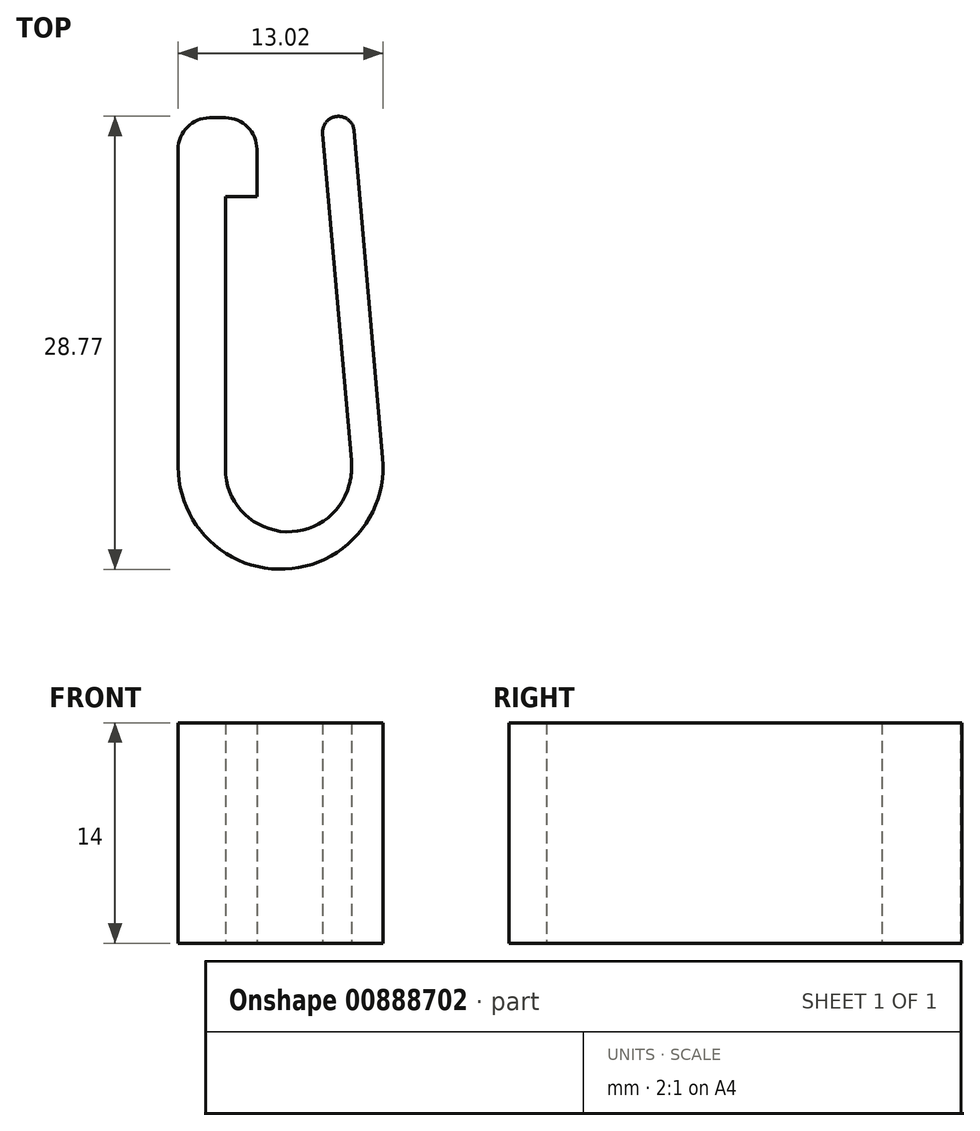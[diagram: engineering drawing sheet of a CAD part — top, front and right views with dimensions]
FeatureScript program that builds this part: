
annotation { "Feature Type Name" : "Feature", "Feature Type Description" : "" }
export const myFeature = defineFeature(function(context is Context, id is Id, definition is map)
    precondition{}
    {
        {
            var Q0;
            Q0=qCreatedBy(makeId("Top.planeOp"),FACE);
            var sketch = newSketch(context, id + "F0", { "sketchPlane" : qUnion([Q0])});
            skLineSegment(sketch, "E0", {"start": v(0, 0) * mm, "end": v(3, 0) * mm});
            skLineSegment(sketch, "E1", {"start": v(5, 2) * mm, "end": v(5, 3) * mm});
            skLineSegment(sketch, "E2", {"start": v(3, 5) * mm, "end": v(-17.17, 5) * mm});
            skLineSegment(sketch, "E3", {"start": v(0, 0) * mm, "end": v(0, 2) * mm});
            skLineSegment(sketch, "E4", {"start": v(0, 2) * mm, "end": v(-17.3, 2) * mm});
            skLineSegment(sketch, "E5", {"start": v(4, -4.18) * mm, "end": v(-16.78, -6) * mm});
            skLineSegment(sketch, "E6", {"start": v(4.18, -6.17) * mm, "end": v(-16.6, -8) * mm});
            skLineSegment(sketch, "E7", {"start": v(5.09, -5.1) * mm, "end": v(5.09, -5.1) * mm});
            skArc(sketch, "E8", {"start": v(-18.33, -5.87) * mm, "mid": v(-17.56, -6) * mm, "end": v(-16.78, -6) * mm});
            skArc(sketch, "E9", {"start": v(-17.17, 5) * mm, "mid": v(-23.67, -1.8) * mm, "end": v(-16.6, -8) * mm});
            skPoint(sketch, "E10.visualSharp", {"position": v(5, -4.1) * mm});
            skArc(sketch, "E10.filletArc", {"start": v(5.09, -5.1) * mm, "mid": v(4.73, -4.41) * mm, "end": v(4, -4.18) * mm});
            skPoint(sketch, "E11.visualSharp", {"position": v(5.17, -6.09) * mm});
            skArc(sketch, "E11.filletArc", {"start": v(4.18, -6.17) * mm, "mid": v(4.86, -5.82) * mm, "end": v(5.09, -5.1) * mm});
            skPoint(sketch, "E12.visualSharp", {"position": v(5, 0) * mm});
            skArc(sketch, "E12.filletArc", {"start": v(3, 0) * mm, "mid": v(4.41, 0.59) * mm, "end": v(5, 2) * mm});
            skPoint(sketch, "E13.visualSharp", {"position": v(5, 5) * mm});
            skArc(sketch, "E13.filletArc", {"start": v(5, 3) * mm, "mid": v(4.41, 4.41) * mm, "end": v(3, 5) * mm});
            skPoint(sketch, "E14.visualSharp", {"position": v(-20, 2) * mm});
            skArc(sketch, "E14.filletArc", {"start": v(-17.3, 2) * mm, "mid": v(-21.27, -1.48) * mm, "end": v(-18.33, -5.87) * mm});
            skSolve(sketch);
        }
        {
            var Q0;
            Q0=makeQuery(id+"F0.imprint","IMPRINT",FACE,{"disambiguationData":[TD([[makeQuery(id+"F0.imprint","IMPRINT",EDGE,{"derivedFrom":sQuery(id+"F0.wireOp",EDGE,"E0")}),1.0]])]});
            extrude(context, id + "F1", {"entities" : qUnion([Q0]), "depth" : 14 * mm, "offsetDistance" : 25 * mm});
        }
        {
            var Q0;
            Q0=makeQuery(id+"F1.opExtrude","SWEPT_BODY",BODY,{"disambiguationData":[OSD([sQuery(id+"F0.wireOp",EDGE,"E0"),sQuery(id+"F0.wireOp",EDGE,"E1"),sQuery(id+"F0.wireOp",EDGE,"E2"),sQuery(id+"F0.wireOp",EDGE,"E3"),sQuery(id+"F0.wireOp",EDGE,"E4"),sQuery(id+"F0.wireOp",EDGE,"E5"),sQuery(id+"F0.wireOp",EDGE,"E6"),sQuery(id+"F0.wireOp",EDGE,"E8"),sQuery(id+"F0.wireOp",EDGE,"E9"),sQuery(id+"F0.wireOp",EDGE,"E10.filletArc"),sQuery(id+"F0.wireOp",EDGE,"E11.filletArc"),sQuery(id+"F0.wireOp",EDGE,"E12.filletArc"),sQuery(id+"F0.wireOp",EDGE,"E13.filletArc"),sQuery(id+"F0.wireOp",EDGE,"E14.filletArc")])]});
            var Q1;
            Q1=makeQuery(id+"F1.opExtrude","SWEPT_EDGE",EDGE,{"disambiguationData":[OSD([sQuery(id+"F0.wireOp",EDGE,"E3"),sQuery(id+"F0.wireOp",EDGE,"E4")])]});
            var Q2;
            Q2=makeQuery(id+"F1.opExtrude","SWEPT_EDGE",EDGE,{"disambiguationData":[OSD([sQuery(id+"F0.wireOp",EDGE,"E4"),sQuery(id+"F0.wireOp",EDGE,"E14.filletArc")])]});
            transform(context, id + "F2", {"entities" : qUnion([Q0]), "transformType" : TransformType.ROTATION, "transformAxis" : qUnion([Q2]), "angle" : 270 * degree, "makeCopy" : false});
        }
    });
